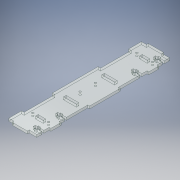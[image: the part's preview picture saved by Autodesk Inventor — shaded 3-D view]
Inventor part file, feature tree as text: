
AUTODESK INVENTOR PART (.ipt)
format: ipt  version: 2019 (Build 230136000, 136)  size: 496,128 bytes
history: native  units: mm
features: extrude x7, sketch x7, projected_geometry x6
ambient origin geometry x8: Origin, YZ Plane, XZ Plane, XY Plane, X Axis, Y Axis, Z Axis, Center Point
bodies: Solid1 (feature_tree)
feature tree (20):
  extrude  "Extrusion1"  Depth=260.0mm
  extrude  "Extrusion2"  Depth=25.0mm
  extrude  "Extrusion3"  Depth=25.0mm
  extrude  "Extrusion4"  Depth=90.0mm
  extrude  "Extrusion5"  Depth=15.0mm
  extrude  "Extrusion6"  Depth=35.0mm
  extrude  "Extrusion7"  Depth=5.0mm TaperAngle=0.0deg
  sketch  "Sketch1"  dims[d0=50.0mm d1=260.0mm]
  sketch  "Sketch2"  dims[d2=5.0mm d3=25.0mm]
  projected_geometry  "Projected Loop1"
  sketch  "Sketch3"  dims[d4=5.0mm d5=25.0mm]
  projected_geometry  "Projected Loop2"
  sketch  "Sketch4"  dims[d7=5.0mm d8=90.0mm]
  projected_geometry  "Projected Loop3"
  sketch  "Sketch5"  dims[d9=5.0mm d10=0.0mm d11=15.0mm]
  projected_geometry  "Projected Loop4"
  sketch  "Sketch6"  dims[d12=5.0mm d13=35.0mm]
  projected_geometry  "Projected Loop5"
  sketch  "Sketch7"  dims[d14=17.5mm d15=5.0mm d16=0.0mm d17=5.0mm d18=15.0mm d19=26.0mm d20=4.0mm d21=4.0mm d23=15.0mm d24=15.0mm d25=25.0mm d26=25.0mm d27=5.0mm d28=0.0mm d29=60.0mm d30=60.0mm d31=17.5mm d32=4.0mm d33=4.0mm d34=8.0mm d35=8.0mm d36=4.0mm d37=4.0mm d38=8.0mm d39=8.0mm d42=25.0mm d43=5.0mm d44=90.0mm d45=10.0mm d46=0.0mm d47=15.0mm d48=4.0mm d49=4.0mm d50=8.0mm d51=4.0mm d52=10.0mm d53=15.0mm d54=4.0mm d55=4.0mm d56=8.0mm d57=4.0mm d58=40.0mm d59=3.5mm d60=20.0mm d61=10.0mm d62=15.0mm d63=4.0mm d64=4.0mm d65=8.0mm d66=4.0mm d67=15.0mm d68=4.0mm d69=4.0mm d70=8.0mm d71=4.0mm d72=40.0mm d73=3.5mm d74=20.0mm d75=10.0mm d76=10.0mm d77=3.5mm d78=60.0mm d79=30.0mm d80=5.0mm d81=0.0mm d82=17.0mm d83=4.0mm d84=4.0mm d85=8.0mm d86=10.0mm d87=17.0mm d88=4.0mm d89=4.0mm d90=8.0mm d91=17.0mm d92=4.0mm d93=4.0mm d94=8.0mm d95=17.0mm d96=4.0mm d97=4.0mm d98=8.0mm d99=10.0mm d100=10.0mm d101=10.0mm d102=5.0mm d103=0.0mm d104=30.0mm d105=3.5mm d106=10.0mm d107=30.0mm d108=3.5mm d109=10.0mm d110=5.0mm d111=0.0mm d112=0.0mm d113=0.0mm d114=4.0mm d115=4.0mm d116=0.0mm d117=4.0mm d118=0.0mm d119=4.0mm]
  projected_geometry  "Projected Loop6"
